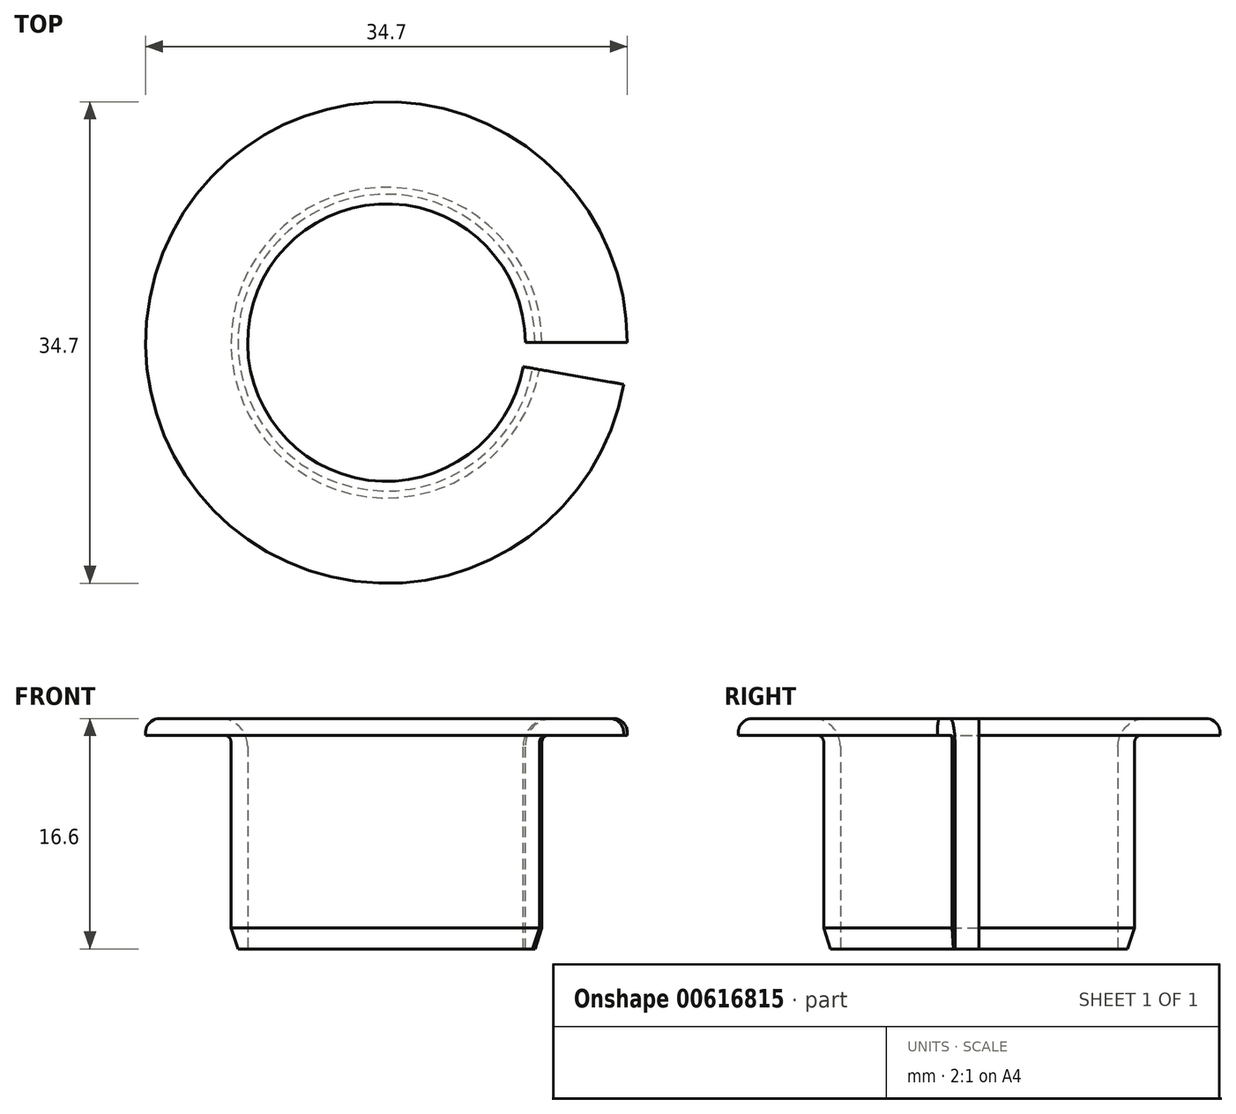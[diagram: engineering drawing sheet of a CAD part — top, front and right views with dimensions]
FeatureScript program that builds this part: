
annotation { "Feature Type Name" : "Feature", "Feature Type Description" : "" }
export const myFeature = defineFeature(function(context is Context, id is Id, definition is map)
    precondition{}
    {
        {
            var Q0;
            Q0=qCreatedBy(makeId("Front.planeOp"),FACE);
            var sketch = newSketch(context, id + "F0", { "sketchPlane" : qUnion([Q0])});
            skLineSegment(sketch, "E0", {"start": v(10, 0) * mm, "end": v(10, 14.6) * mm});
            skLineSegment(sketch, "E1", {"start": v(12, 16.6) * mm, "end": v(16.35, 16.6) * mm});
            skLineSegment(sketch, "E2", {"start": v(17.35, 15.6) * mm, "end": v(17.35, 15.4) * mm});
            skLineSegment(sketch, "E3", {"start": v(17.35, 15.4) * mm, "end": v(11.7, 15.4) * mm});
            skLineSegment(sketch, "E4", {"start": v(11.2, 14.9) * mm, "end": v(11.2, 1.5) * mm});
            skLineSegment(sketch, "E5", {"start": v(11.2, 1.5) * mm, "end": v(10.7, 0) * mm});
            skLineSegment(sketch, "E6", {"start": v(10.7, 0) * mm, "end": v(10, 0) * mm});
            skLineSegment(sketch, "E7", {"start": v(0, 0) * mm, "end": v(0, 48.77) * mm, "construction": true});
            skPoint(sketch, "E8.visualSharp", {"position": v(17.35, 16.6) * mm});
            skArc(sketch, "E8.filletArc", {"start": v(17.35, 15.6) * mm, "mid": v(17.06, 16.3) * mm, "end": v(16.35, 16.6) * mm});
            skPoint(sketch, "E9.visualSharp", {"position": v(10, 16.6) * mm});
            skArc(sketch, "E9.filletArc", {"start": v(12, 16.6) * mm, "mid": v(10.59, 16.01) * mm, "end": v(10, 14.6) * mm});
            skPoint(sketch, "E10.visualSharp", {"position": v(11.2, 15.4) * mm});
            skArc(sketch, "E10.filletArc", {"start": v(11.7, 15.4) * mm, "mid": v(11.35, 15.25) * mm, "end": v(11.2, 14.9) * mm});
            skSolve(sketch);
        }
        {
            var Q0;
            Q0=makeQuery(id+"F0.imprint","IMPRINT",FACE,{"disambiguationData":[TD([[makeQuery(id+"F0.imprint","IMPRINT",EDGE,{"derivedFrom":sQuery(id+"F0.wireOp",EDGE,"E0")}),-1.0]])]});
            var Q1;
            Q1=sQuery(id+"F0.wireOp",EDGE,"E7");
            revolve(context, id + "F1", {"surfaceOperationType" : NewSurfaceOperationType.NEW, "entities" : qUnion([Q0]), "axis" : qUnion([Q1]), "revolveType" : RevolveType.ONE_DIRECTION, "angle" : 350 * degree});
        }
    });
